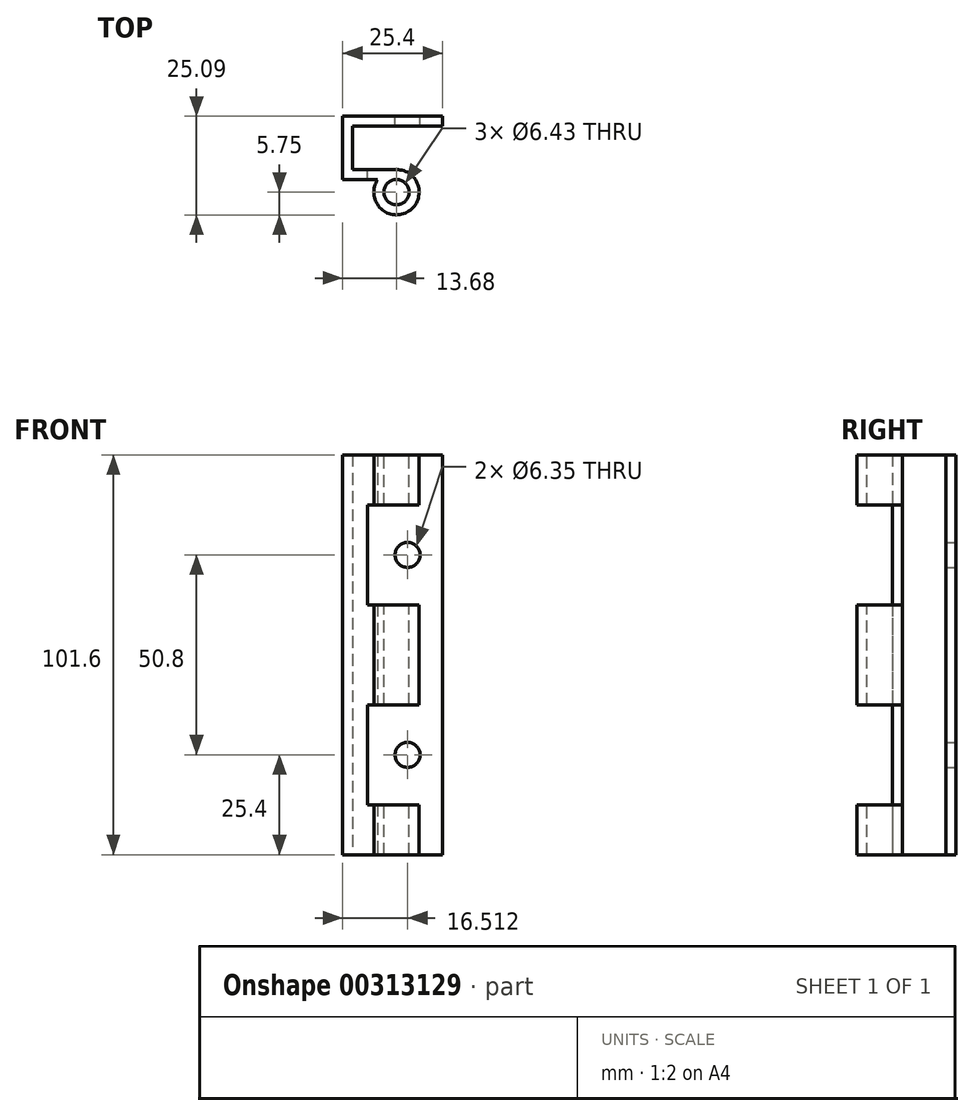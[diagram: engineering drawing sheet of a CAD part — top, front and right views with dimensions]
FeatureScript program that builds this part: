
annotation { "Feature Type Name" : "Feature", "Feature Type Description" : "" }
export const myFeature = defineFeature(function(context is Context, id is Id, definition is map)
    precondition{}
    {
        {
            var Q0;
            Q0=qCreatedBy(makeId("Top.planeOp"),FACE);
            var sketch = newSketch(context, id + "F0", { "sketchPlane" : qUnion([Q0])});
            skLineSegment(sketch, "E0", {"start": v(0, 5.75) * mm, "end": v(-11.14, 5.75) * mm});
            skLineSegment(sketch, "E1", {"start": v(-11.14, 5.75) * mm, "end": v(-11.14, 16.8) * mm});
            skLineSegment(sketch, "E2", {"start": v(-11.14, 16.8) * mm, "end": v(11.72, 16.8) * mm});
            skLineSegment(sketch, "E3", {"start": v(11.72, 16.8) * mm, "end": v(11.72, 19.34) * mm});
            skLineSegment(sketch, "E4", {"start": v(11.72, 19.34) * mm, "end": v(-13.68, 19.34) * mm});
            skLineSegment(sketch, "E5", {"start": v(-13.68, 19.34) * mm, "end": v(-13.68, 3.21) * mm});
            skLineSegment(sketch, "E6", {"start": v(-13.68, 3.21) * mm, "end": v(-4.77, 3.21) * mm});
            skArc(sketch, "E7", {"start": v(-4.77, 3.21) * mm, "mid": v(2.7, -5.08) * mm, "end": v(0, 5.75) * mm});
            skSolve(sketch);
        }
        {
            var Q0;
            Q0=qSketchRegion(id+"F0",true);
            extrude(context, id + "F1", {"entities" : qUnion([Q0]), "endBound" : BoundingType.SYMMETRIC, "depth" : 101.6 * mm});
        }
        {
            var Q0;
            Q0=makeQuery(id+"F1.opExtrude","SWEPT_FACE",FACE,{"disambiguationData":[OSD([sQuery(id+"F0.wireOp",EDGE,"E0")])]});
            var sketch = newSketch(context, id + "F2", { "sketchPlane" : qUnion([Q0])});
            skLineSegment(sketch, "E8.bottom", {"start": v(7.33, 38.1) * mm, "end": v(-18.07, 38.1) * mm});
            skLineSegment(sketch, "E8.top", {"start": v(7.33, 12.7) * mm, "end": v(-18.07, 12.7) * mm});
            skLineSegment(sketch, "E8.left", {"start": v(7.33, 38.1) * mm, "end": v(7.33, 12.7) * mm});
            skLineSegment(sketch, "E8.right", {"start": v(-18.07, 38.1) * mm, "end": v(-18.07, 12.7) * mm});
            skLineSegment(sketch, "E9.bottom", {"start": v(7.33, -38.1) * mm, "end": v(-18.07, -38.1) * mm});
            skLineSegment(sketch, "E9.top", {"start": v(7.33, -12.7) * mm, "end": v(-18.07, -12.7) * mm});
            skLineSegment(sketch, "E9.left", {"start": v(7.33, -38.1) * mm, "end": v(7.33, -12.7) * mm});
            skLineSegment(sketch, "E9.right", {"start": v(-18.07, -38.1) * mm, "end": v(-18.07, -12.7) * mm});
            skSolve(sketch);
        }
        {
            var Q0;
            Q0 = qSketchRegion(id + "F2", true);
            extrude(context, id + "F3", {"entities" : qUnion([Q0]), "operationType" : NewBodyOperationType.REMOVE, "endBound" : BoundingType.THROUGH_ALL, "oppositeDirection" : true, "depth" : 25.4 * mm});
        }
        {
            var Q0;
            Q0=makeQuery(id+"F1.opExtrude","CAP_FACE",FACE,{"disambiguationData":[OSD([sQuery(id+"F0.wireOp",EDGE,"E0"),sQuery(id+"F0.wireOp",EDGE,"E1"),sQuery(id+"F0.wireOp",EDGE,"E2"),sQuery(id+"F0.wireOp",EDGE,"E3"),sQuery(id+"F0.wireOp",EDGE,"E4"),sQuery(id+"F0.wireOp",EDGE,"E5"),sQuery(id+"F0.wireOp",EDGE,"E6"),sQuery(id+"F0.wireOp",EDGE,"E7")])],"isStart":false});
            var sketch = newSketch(context, id + "F4", { "sketchPlane" : qUnion([Q0])});
            skCircle(sketch, "E10", {"center": v(0, 0) * mm, "radius": 3.21 * mm});
            skSolve(sketch);
        }
        {
            var Q0;
            Q0 = qSketchRegion(id + "F4", true);
            extrude(context, id + "F5", {"entities" : qUnion([Q0]), "operationType" : NewBodyOperationType.REMOVE, "endBound" : BoundingType.THROUGH_ALL, "oppositeDirection" : true, "depth" : 25.4 * mm});
        }
        {
            var Q0;
            Q0=makeQuery(id+"F1.opExtrude","SWEPT_FACE",FACE,{"disambiguationData":[OSD([sQuery(id+"F0.wireOp",EDGE,"E4")])]});
            var sketch = newSketch(context, id + "F6", { "sketchPlane" : qUnion([Q0])});
            skCircle(sketch, "E11", {"center": v(-2.83, 25.4) * mm, "radius": 3.18 * mm});
            skCircle(sketch, "E12", {"center": v(-2.83, -25.4) * mm, "radius": 3.18 * mm});
            skSolve(sketch);
        }
        {
            var Q0;
            Q0 = qSketchRegion(id + "F6", true);
            extrude(context, id + "F7", {"entities" : qUnion([Q0]), "operationType" : NewBodyOperationType.REMOVE, "endBound" : BoundingType.UP_TO_NEXT, "oppositeDirection" : true, "depth" : 25.4 * mm});
        }
    });
